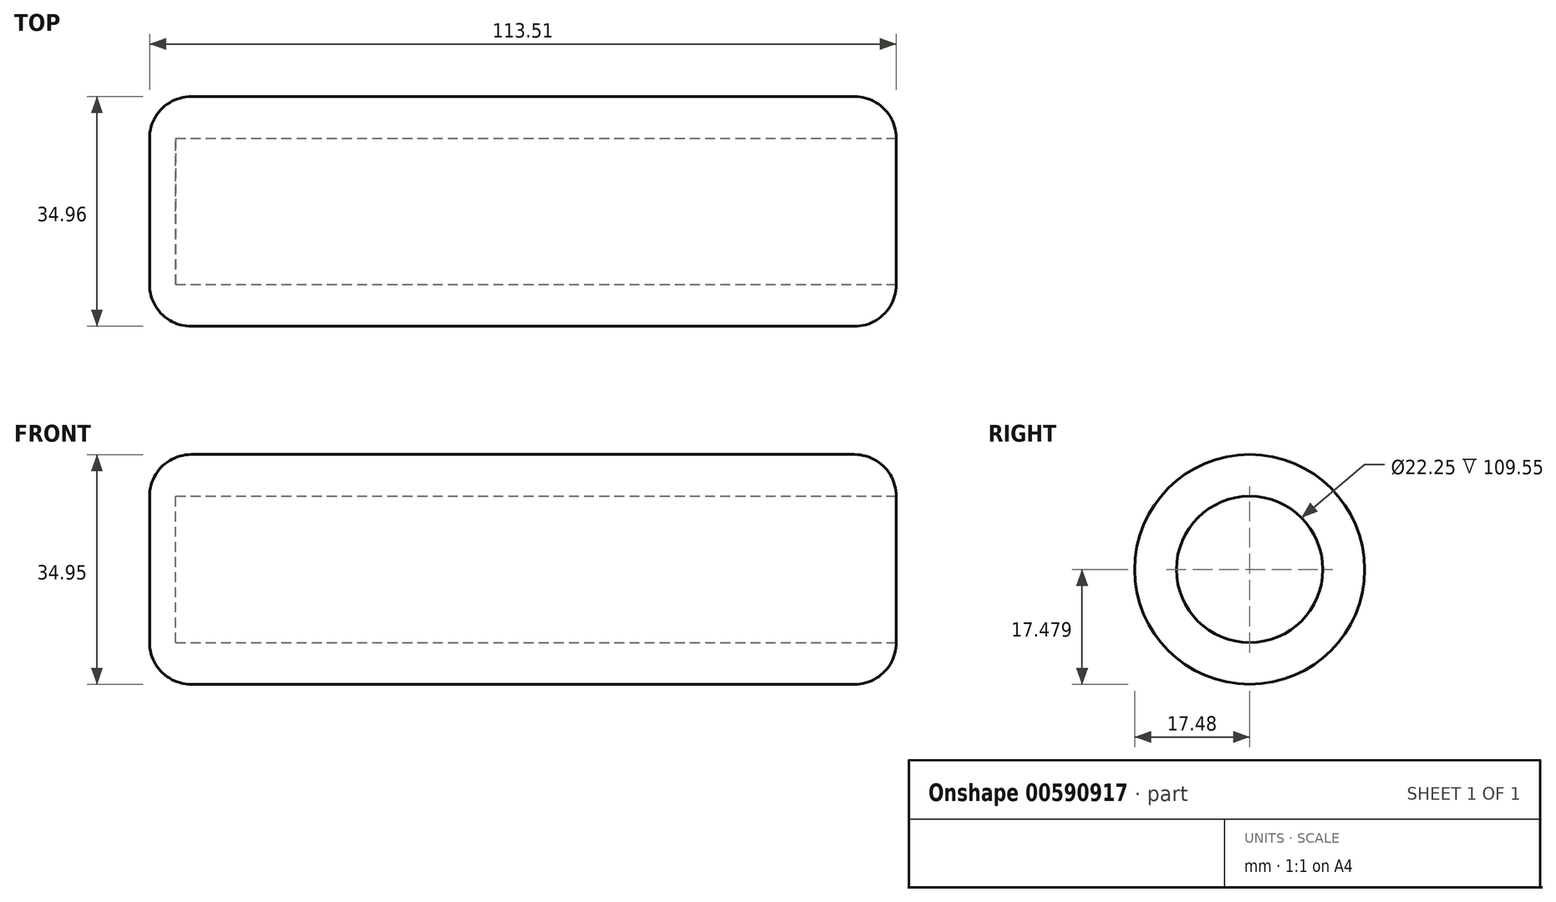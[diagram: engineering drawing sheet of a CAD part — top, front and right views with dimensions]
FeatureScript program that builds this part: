
annotation { "Feature Type Name" : "Feature", "Feature Type Description" : "" }
export const myFeature = defineFeature(function(context is Context, id is Id, definition is map)
    precondition{}
    {
        {
            var Q0;
            Q0=qCreatedBy(makeId("Front.planeOp"),FACE);
            var sketch = newSketch(context, id + "F0", { "sketchPlane" : qUnion([Q0])});
            skLineSegment(sketch, "E0", {"start": v(0, -2.38) * mm, "end": v(0, -19.86) * mm});
            skLineSegment(sketch, "E1", {"start": v(0, -19.86) * mm, "end": v(113.51, -19.86) * mm});
            skLineSegment(sketch, "E2", {"start": v(113.51, -19.86) * mm, "end": v(113.51, -13.5) * mm});
            skLineSegment(sketch, "E3", {"start": v(113.51, -13.5) * mm, "end": v(3.96, -13.5) * mm});
            skLineSegment(sketch, "E4", {"start": v(3.96, -13.5) * mm, "end": v(3.96, -2.38) * mm});
            skLineSegment(sketch, "E5", {"start": v(3.96, -2.38) * mm, "end": v(0, -2.38) * mm});
            skSolve(sketch);
        }
        {
            var Q0;
            Q0=makeQuery(id+"F0.imprint","IMPRINT",FACE,{"disambiguationData":[TD([[makeQuery(id+"F0.imprint","IMPRINT",EDGE,{"derivedFrom":sQuery(id+"F0.wireOp",EDGE,"E0")}),1.0]])]});
            var Q1;
            Q1=sQuery(id+"F0.wireOp",EDGE,"E5");
            revolve(context, id + "F1", {"entities" : qUnion([Q0]), "axis" : qUnion([Q1]), "revolveType" : RevolveType.FULL});
        }
        {
            var Q0;
            Q0=makeQuery(id+"F1.opRevolve","SWEPT_FACE",FACE,{"disambiguationData":[OSD([sQuery(id+"F0.wireOp",EDGE,"E1")])]});
            fillet(context, id + "F2", {"entities" : qUnion([Q0]), "radius" : 6.35 * mm, "tangentPropagation" : true, "allowEdgeOverflow" : false});
        }
    });
